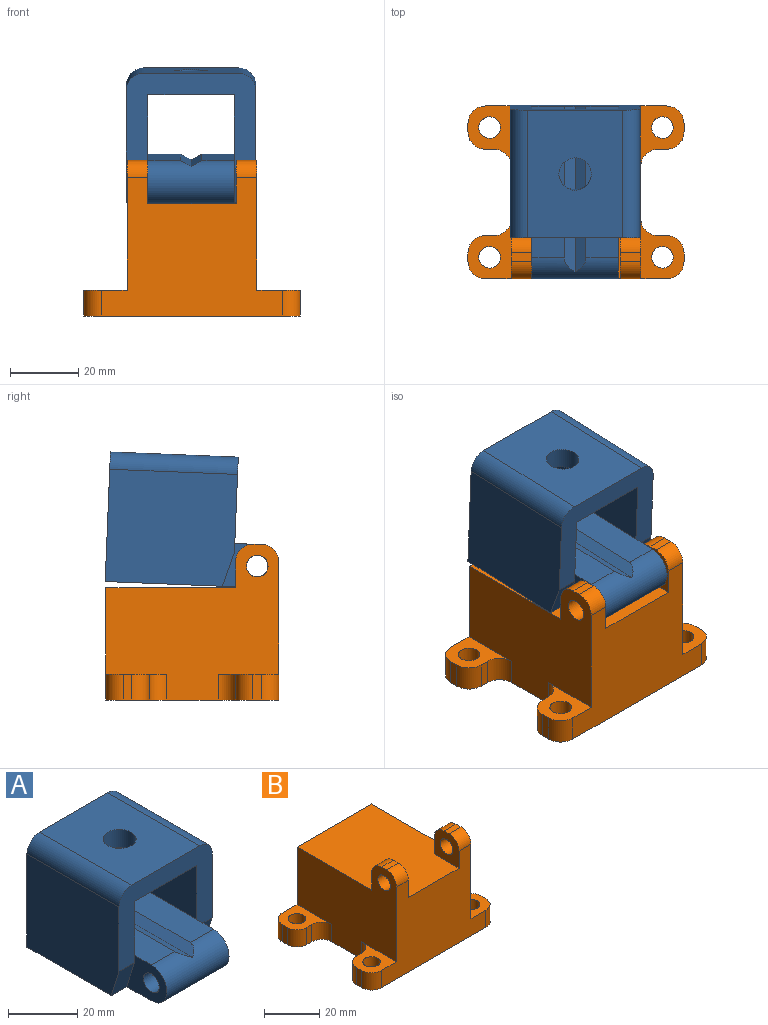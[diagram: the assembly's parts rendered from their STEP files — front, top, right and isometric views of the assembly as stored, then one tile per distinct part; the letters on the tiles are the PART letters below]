
ASSEMBLY  parts=2 mates=1
PART A: 23 faces, bbox 39.6x52.3x39.6 mm
  f0: plane 44.45x9.53mm, normal (0,0,1), area 423.4mm2, adj f3,f7,f12,f14,f19
  f1: plane 44.45x9.53mm, normal (0,0,1), area 423.6mm2, adj f4,f7,f13,f17,f19
  f2: plane 37.59x33.02mm, normal (-1,0,0), area 1225.2mm2, adj f5,f7,f8,f11,f21
  f3: plane 16.38x12.7mm, normal (-1,0,0), area 134.9mm2, adj f0,f5,f8,f9,f11,f19
  f4: plane 16.38x12.7mm, normal (1,0,0), area 134.9mm2, adj f1,f5,f8,f9,f10,f19
  f5: plane 38.11x27.94mm, normal (0,-1,0), area 505.1mm2, adj f2,f3,f4,f6,f10,f11,f14,f15
  f6: plane 37.6x12.71mm, normal (1,0,0), area 461.3mm2, adj f5,f7,f8,f10,f16
  f7: plane 38.11x38.1mm, normal (0,1,0), area 951.7mm2, adj f0,f1,f2,f6,f8,f12,f13,f14
  f8: plane 44.45x38.1mm, normal (0,0,-1), area 1566.1mm2, adj f2,f3,f4,f6,f7,f10,f11,f19
  f9: cylinder r=3.17mm len=25.4mm, axis (-1,0,0), area 506.7mm2, adj f3,f4
  f10: plane 10.16x6.35mm, normal (0,-0.95,-0.3), area 67.6mm2, adj f4,f5,f6,f8
  f11: plane 10.16x6.35mm, normal (0,-0.95,-0.3), area 67.6mm2, adj f2,f3,f5,f8
  f12: plane 50.18x4.71mm, normal (0.45,0,0.89), area 168mm2, adj f0,f7,f13,f19
  f13: plane 50.18x4.71mm, normal (-0.45,0,0.89), area 168mm2, adj f1,f7,f12,f19
  f14: plane 37.59x19.05mm, normal (1,0,0), area 716.1mm2, adj f0,f5,f7,f18
  f15: plane 37.59x27.95mm, normal (0,0,1), area 979.3mm2, adj f5,f7,f20,f21,f22
  f16: plane 37.6x20.33mm, normal (1,0,0), area 763.9mm2, adj f5,f6,f7,f20
  f17: plane 37.59x19.05mm, normal (-1,0,0), area 716.1mm2, adj f1,f5,f7,f18
  f18: plane 37.59x25.41mm, normal (0,0,-1), area 883.8mm2, adj f5,f7,f14,f17,f22
  f19: cylinder r=6.35mm len=25.4mm, axis (1,0,0), area 492.1mm2, adj f0,f1,f3,f4,f8,f12,f13
  f20: cylinder r=5.08mm len=37.59mm, axis (0,-1,0), area 300mm2, adj f5,f7,f15,f16
  f21: cylinder r=5.08mm len=37.59mm, axis (0,1,0), area 300mm2, adj f2,f5,f7,f15
  f22: cylinder r=4.76mm len=9.53mm, axis (0,0,1), area 190mm2, adj f15,f18
PART B: 46 faces, bbox 63.5x50.8x45.7 mm
  f0: plane 50.8x38.1mm, normal (0,0,1), area 1780.6mm2, adj f1,f7,f12,f17,f22,f23,f25,f26
  f1: plane 53.34x33.02mm, normal (0,1,0), area 1374.2mm2, adj f0,f5,f6,f12,f16,f17,f34,f44
  f2: plane 7.62x2.54mm, normal (0,-1,0), area 19.4mm2, adj f5,f6,f35,f36
  f3: plane 7.62x2.54mm, normal (1,0,0), area 19.4mm2, adj f5,f6,f34,f35
  f4: cylinder r=3.17mm len=7.62mm, axis (0,0,-1), area 152mm2, adj f5,f6
  f5: plane 17.78x12.7mm, normal (0,0,1), area 124.1mm2, adj f1,f2,f3,f4,f12,f34,f35,f36
  f6: plane 63.5x50.8mm, normal (0,0,-1), area 2431.8mm2, adj f1,f2,f3,f4,f7,f8,f9,f10
  f7: plane 53.34x40.64mm, normal (0,-1,0), area 1467.1mm2, adj f0,f6,f11,f12,f17,f21,f23,f26
  f8: plane 7.62x2.54mm, normal (1,0,0), area 19.4mm2, adj f6,f11,f38,f39
  f9: plane 7.62x2.54mm, normal (0,1,0), area 19.4mm2, adj f6,f11,f37,f38
  f10: cylinder r=3.17mm len=7.62mm, axis (0,0,-1), area 152mm2, adj f6,f11
  f11: plane 17.78x12.7mm, normal (0,0,1), area 124.1mm2, adj f7,f8,f9,f10,f12,f37,f38,f39
  f12: plane 50.8x45.72mm, normal (1,0,0), area 1525mm2, adj f0,f1,f5,f6,f7,f11,f25,f27
  f13: plane 7.62x2.54mm, normal (0,-1,0), area 19.4mm2, adj f6,f16,f43,f45
  f14: cylinder r=3.17mm len=7.62mm, axis (0,0,-1), area 152mm2, adj f6,f16
  f15: plane 7.62x2.54mm, normal (-1,0,0), area 19.4mm2, adj f6,f16,f43,f44
  f16: plane 17.78x12.7mm, normal (0,0,1), area 124.1mm2, adj f1,f13,f14,f15,f17,f43,f44,f45
  f17: plane 50.8x45.72mm, normal (-1,0,0), area 1525mm2, adj f0,f1,f6,f7,f16,f21,f22,f24
  f18: plane 7.62x2.54mm, normal (0,1,0), area 19.4mm2, adj f6,f21,f40,f41
  f19: cylinder r=3.17mm len=7.62mm, axis (0,0,-1), area 152mm2, adj f6,f21
  f20: plane 7.62x2.54mm, normal (-1,0,0), area 19.4mm2, adj f6,f21,f41,f42
  f21: plane 17.78x12.7mm, normal (0,0,1), area 124.1mm2, adj f7,f17,f18,f19,f20,f40,f41,f42
  f22: plane 7.62x6.1mm, normal (0,1,0), area 46.5mm2, adj f0,f17,f23,f33
  f23: plane 12.7x12.7mm, normal (1,0,0), area 118.5mm2, adj f0,f7,f22,f24,f29,f32,f33
  f24: plane 6.1x2.54mm, normal (0,0,1), area 15.5mm2, adj f17,f23,f32,f33
  f25: plane 7.62x6.1mm, normal (0,1,0), area 46.5mm2, adj f0,f12,f26,f30
  f26: plane 12.7x12.7mm, normal (-1,0,0), area 118.5mm2, adj f0,f7,f25,f27,f28,f30,f31
  f27: plane 6.1x2.54mm, normal (0,0,1), area 15.5mm2, adj f12,f26,f30,f31
  f28: cylinder r=3.17mm len=6.35mm, axis (-1,0,0), area 121.6mm2, adj f12,f26
  f29: cylinder r=3.17mm len=6.35mm, axis (-1,0,0), area 121.6mm2, adj f17,f23
  f30: cylinder r=5.08mm len=6.1mm, axis (1,0,0), area 48.6mm2, adj f12,f25,f26,f27
  f31: cylinder r=5.08mm len=6.1mm, axis (1,0,0), area 48.6mm2, adj f7,f12,f26,f27
  f32: cylinder r=5.08mm len=6.1mm, axis (1,0,0), area 48.6mm2, adj f7,f17,f23,f24
  f33: cylinder r=5.08mm len=6.1mm, axis (1,0,0), area 48.6mm2, adj f17,f22,f23,f24
  f34: cylinder r=5.08mm len=7.62mm, axis (0,0,-1), area 60.8mm2, adj f1,f3,f5,f6
  f35: cylinder r=5.08mm len=7.62mm, axis (0,0,1), area 60.8mm2, adj f2,f3,f5,f6
  f36: cylinder r=5.08mm len=7.62mm, axis (0,0,1), area 60.8mm2, adj f2,f5,f6,f12
  f37: cylinder r=5.08mm len=7.62mm, axis (0,0,-1), area 60.8mm2, adj f6,f9,f11,f12
  f38: cylinder r=5.08mm len=7.62mm, axis (0,0,1), area 60.8mm2, adj f6,f8,f9,f11
  f39: cylinder r=5.08mm len=7.62mm, axis (0,0,-1), area 60.8mm2, adj f6,f7,f8,f11
  f40: cylinder r=5.08mm len=7.62mm, axis (0,0,-1), area 60.8mm2, adj f6,f17,f18,f21
  f41: cylinder r=5.08mm len=7.62mm, axis (0,0,1), area 60.8mm2, adj f6,f18,f20,f21
  f42: cylinder r=5.08mm len=7.62mm, axis (0,0,1), area 60.8mm2, adj f6,f7,f20,f21
  f43: cylinder r=5.08mm len=7.62mm, axis (0,0,1), area 60.8mm2, adj f6,f13,f15,f16
  f44: cylinder r=5.08mm len=7.62mm, axis (0,0,1), area 60.8mm2, adj f1,f6,f15,f16
  f45: cylinder r=5.08mm len=7.62mm, axis (0,0,1), area 60.8mm2, adj f6,f13,f16,f17
PLACE A rot(axis=(1,0,0),2.3deg) t=(19.67,23.32,14.5)mm
PLACE B t=(19.93,23.08,-19.3)mm fixed
MATE revolute B.f28 <-> A.f19  axis (-1,0,0) through (6.97,4.03,20.07)mm
